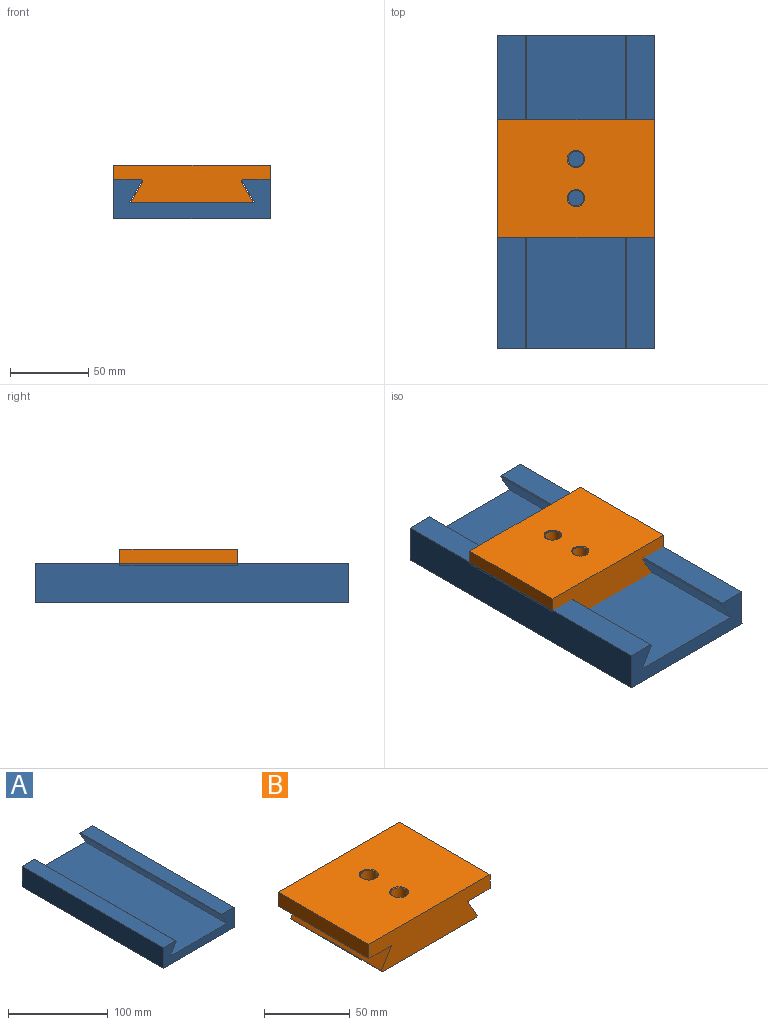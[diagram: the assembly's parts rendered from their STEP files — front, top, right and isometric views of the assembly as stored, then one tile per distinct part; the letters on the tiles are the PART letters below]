
ASSEMBLY  parts=2 mates=1
PART A: 12 faces, bbox 100x200x25 mm
  f0: plane 200x14.13mm, normal (0.87,0,-0.5), area 3264.1mm2, adj f7,f8,f9,f11
  f1: plane 200x17.66mm, normal (0,0,1), area 3532.1mm2, adj f2,f8,f9,f11
  f2: plane 200x25mm, normal (-1,0,0), area 5000mm2, adj f1,f3,f8,f9
  f3: plane 200x100mm, normal (0,0,-1), area 20000mm2, adj f2,f4,f8,f9
  f4: plane 200x25mm, normal (1,0,0), area 5000mm2, adj f3,f5,f8,f9
  f5: plane 200x17.66mm, normal (0,0,1), area 3532.1mm2, adj f4,f8,f9,f10
  f6: plane 200x14.13mm, normal (-0.87,0,-0.5), area 3264.1mm2, adj f7,f8,f9,f10
  f7: plane 200x80mm, normal (0,0,1), area 16000mm2, adj f0,f6,f8,f9
  f8: plane 100x25mm, normal (0,-1,0), area 1429mm2, adj f0,f1,f2,f3,f4,f5,f6,f7
  f9: plane 100x25mm, normal (0,1,0), area 1429mm2, adj f0,f1,f2,f3,f4,f5,f6,f7
  f10: plane 200x0.87mm, normal (-0.87,0,0.5), area 200mm2, adj f5,f6,f8,f9
  f11: plane 200x0.87mm, normal (0.87,0,0.5), area 200mm2, adj f0,f1,f8,f9
PART B: 24 faces, bbox 100x75x25 mm
  f0: plane 78x75mm, normal (0,0,-1), area 5396mm2, adj f10,f11,f16,f17,f22,f23
  f1: cylinder r=5mm len=14mm, axis (0,0,1), area 439.8mm2, adj f18,f21
  f2: cylinder r=5mm len=14mm, axis (0,0,1), area 439.8mm2, adj f19,f20
  f3: plane 75x18.66mm, normal (0,0,-1), area 1399.5mm2, adj f4,f9,f10,f11
  f4: plane 75x10mm, normal (1,0,0), area 750mm2, adj f3,f5,f10,f11
  f5: plane 100x75mm, normal (0,0,1), area 7309.9mm2, adj f4,f6,f10,f11,f18,f19
  f6: plane 75x10mm, normal (-1,0,0), area 750mm2, adj f5,f7,f10,f11
  f7: plane 75x18.66mm, normal (0,0,-1), area 1399.5mm2, adj f6,f8,f10,f11
  f8: plane 75x14.13mm, normal (-0.87,0,0.5), area 1224mm2, adj f7,f10,f11,f23
  f9: plane 75x14.13mm, normal (0.87,0,0.5), area 1224mm2, adj f3,f10,f11,f22
  f10: plane 100x25mm, normal (0,-1,0), area 2069.2mm2, adj f0,f3,f4,f5,f6,f7,f8,f9
  f11: plane 100x25mm, normal (0,1,0), area 2069.2mm2, adj f0,f3,f4,f5,f6,f7,f8,f9
  f12: cylinder r=8mm len=16mm, axis (0,0,-1), area 477.5mm2, adj f13,f16
  f13: plane 16x16mm, normal (0,0,-1), area 106mm2, adj f12,f20
  f14: cylinder r=8mm len=16mm, axis (0,0,-1), area 477.5mm2, adj f15,f17
  f15: plane 16x16mm, normal (0,0,-1), area 106mm2, adj f14,f21
  f16: cone r=8mm half-angle=45deg, axis (0,0,-1), area 36.7mm2, adj f0,f12
  f17: cone r=8mm half-angle=45deg, axis (0,0,-1), area 36.7mm2, adj f0,f14
  f18: cone r=5mm half-angle=45deg, axis (0,0,1), area 23.3mm2, adj f1,f5
  f19: cone r=5mm half-angle=45deg, axis (0,0,1), area 23.3mm2, adj f2,f5
  f20: cone r=5.5mm half-angle=45deg, axis (0,0,-1), area 23.3mm2, adj f2,f13
  f21: cone r=5.5mm half-angle=45deg, axis (0,0,-1), area 23.3mm2, adj f1,f15
  f22: plane 75x0.87mm, normal (0.87,0,-0.5), area 75mm2, adj f0,f9,f10,f11
  f23: plane 75x0.87mm, normal (-0.87,0,-0.5), area 75mm2, adj f0,f8,f10,f11
PLACE A t=(67.94,115,55.28)mm fixed
PLACE B rot(axis=(0,-1,0),0deg) t=(67.94,61.03,54.25)mm
MATE slider A.f8 <-> B.f10  axis (0,-1,0) through (67.94,-85,64.25)mm
